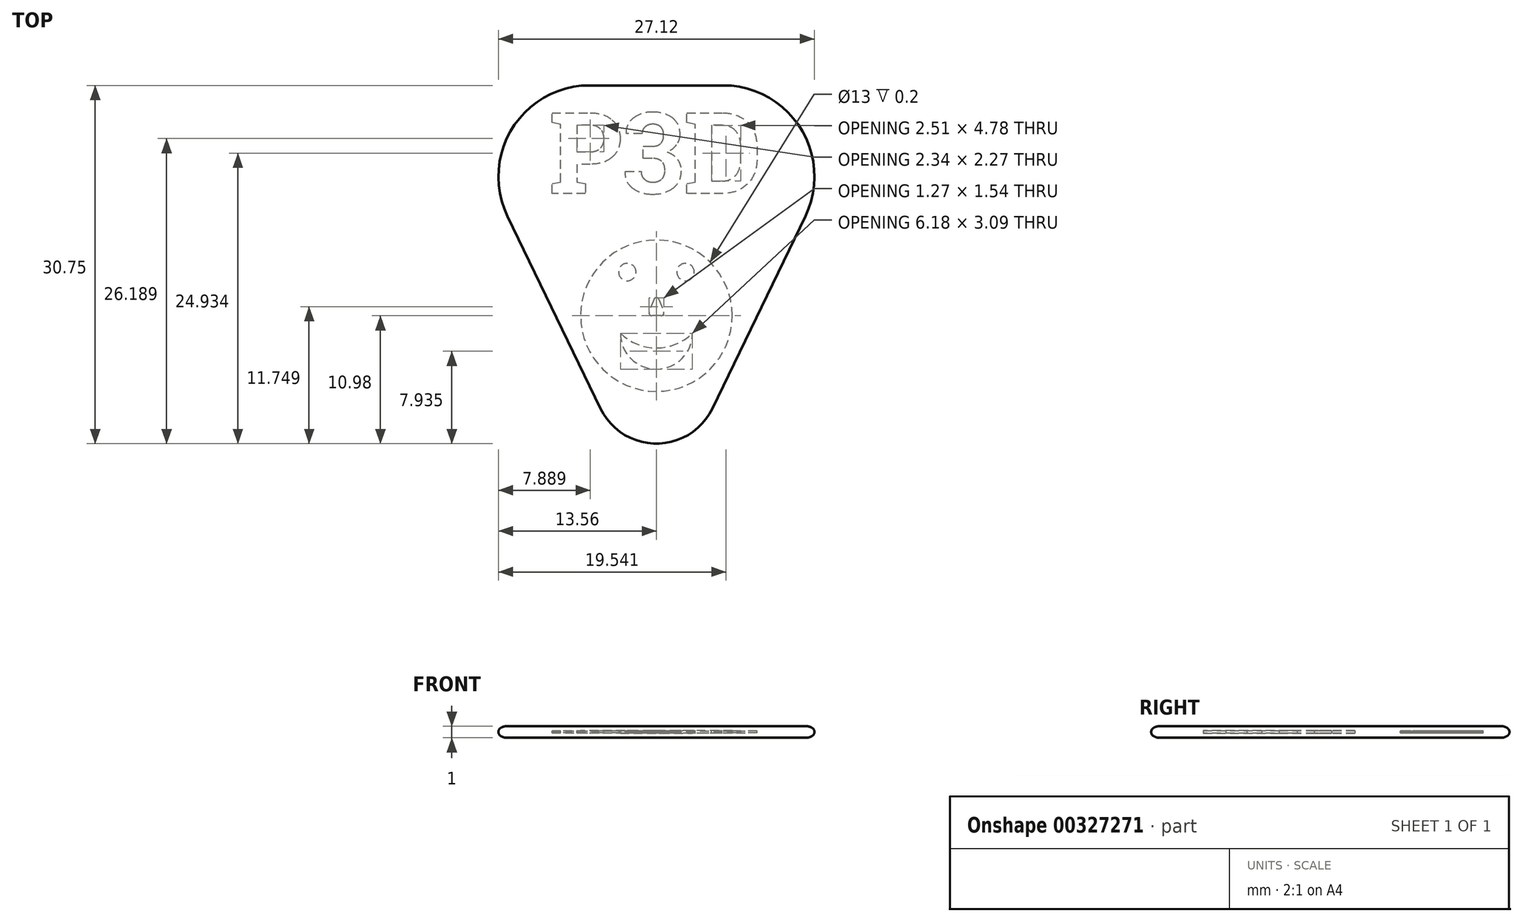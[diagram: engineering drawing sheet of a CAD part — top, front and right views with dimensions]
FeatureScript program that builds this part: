
annotation { "Feature Type Name" : "Feature", "Feature Type Description" : "" }
export const myFeature = defineFeature(function(context is Context, id is Id, definition is map)
    precondition{}
    {
        {
            var Q0;
            Q0=qCreatedBy(makeId("Top.planeOp"),FACE);
            var sketch = newSketch(context, id + "F0", { "sketchPlane" : qUnion([Q0])});
            skLineSegment(sketch, "E0", {"start": v(-5.74, 12.45) * mm, "end": v(5.74, 12.45) * mm});
            skLineSegment(sketch, "E1", {"start": v(12.95, 0.97) * mm, "end": v(4.95, -15.56) * mm});
            skLineSegment(sketch, "E2", {"start": v(-4.95, -15.56) * mm, "end": v(-12.95, 0.97) * mm});
            skPoint(sketch, "E3.visualSharp", {"position": v(-18.5, 12.45) * mm});
            skArc(sketch, "E3.filletArc", {"start": v(-5.74, 12.45) * mm, "mid": v(-12.52, 8.7) * mm, "end": v(-12.95, 0.97) * mm});
            skPoint(sketch, "E4.visualSharp", {"position": v(18.5, 12.45) * mm});
            skArc(sketch, "E4.filletArc", {"start": v(12.95, 0.97) * mm, "mid": v(12.52, 8.7) * mm, "end": v(5.74, 12.45) * mm});
            skPoint(sketch, "E5.visualSharp", {"position": v(0, -25.8) * mm});
            skArc(sketch, "E5.filletArc", {"start": v(-4.95, -15.56) * mm, "mid": v(0, -18.66) * mm, "end": v(4.95, -15.56) * mm});
            skSolve(sketch);
        }
        {
            var Q0;
            Q0=makeQuery(id+"F0.imprint","IMPRINT",FACE,{"disambiguationData":[TD([[makeQuery(id+"F0.imprint","IMPRINT",EDGE,{"derivedFrom":sQuery(id+"F0.wireOp",EDGE,"E0")}),-1.0]])]});
            extrude(context, id + "F1", {"entities" : qUnion([Q0]), "endBound" : BoundingType.SYMMETRIC, "depth" : 1 * mm, "offsetDistance" : 25 * mm});
        }
        {
            var Q0;
            Q0=makeQuery(id+"F1.opExtrude","CAP_EDGE",EDGE,{"disambiguationData":[OSD([sQuery(id+"F0.wireOp",EDGE,"E1")])],"isStart":false});
            var Q1;
            Q1=makeQuery(id+"F1.opExtrude","CAP_EDGE",EDGE,{"disambiguationData":[OSD([sQuery(id+"F0.wireOp",EDGE,"E1")])],"isStart":true});
            chamfer(context, id + "F2", {"entities" : qUnion([Q0, Q1]), "chamferType" : ChamferType.OFFSET_ANGLE, "width" : 0.5 * mm, "oppositeDirection" : false, "angle" : 45 * degree, "tangentPropagation" : true});
        }
        {
            var Q0;
            {var subQ0=sQuery(id+"F0.wireOp",EDGE,"E2");Q0=makeQuery(id+"F2.opChamfer","BLEND_EDGE",EDGE,{"blendedFrom":[makeQuery(id+"F1.opExtrude","CAP_EDGE",EDGE,{"disambiguationData":[OSD([subQ0])],"isStart":false}),makeQuery(id+"F1.opExtrude","CAP_FACE",FACE,{"disambiguationData":[OSD([sQuery(id+"F0.wireOp",EDGE,"E0"),sQuery(id+"F0.wireOp",EDGE,"E1"),subQ0,sQuery(id+"F0.wireOp",EDGE,"E3.filletArc"),sQuery(id+"F0.wireOp",EDGE,"E4.filletArc"),sQuery(id+"F0.wireOp",EDGE,"E5.filletArc")])],"isStart":false})],"blendedInto":[makeQuery(id+"F1.opExtrude","CAP_FACE",FACE,{"disambiguationData":[OSD([sQuery(id+"F0.wireOp",EDGE,"E0"),sQuery(id+"F0.wireOp",EDGE,"E1"),subQ0,sQuery(id+"F0.wireOp",EDGE,"E3.filletArc"),sQuery(id+"F0.wireOp",EDGE,"E4.filletArc"),sQuery(id+"F0.wireOp",EDGE,"E5.filletArc")])],"isStart":false})]});}
            var Q1;
            {var subQ0=sQuery(id+"F0.wireOp",EDGE,"E1");Q1=makeQuery(id+"F2.opChamfer","BLEND_EDGE",EDGE,{"blendedFrom":[makeQuery(id+"F1.opExtrude","CAP_EDGE",EDGE,{"disambiguationData":[OSD([subQ0])],"isStart":true}),makeQuery(id+"F1.opExtrude","CAP_FACE",FACE,{"disambiguationData":[OSD([sQuery(id+"F0.wireOp",EDGE,"E0"),subQ0,sQuery(id+"F0.wireOp",EDGE,"E2"),sQuery(id+"F0.wireOp",EDGE,"E3.filletArc"),sQuery(id+"F0.wireOp",EDGE,"E4.filletArc"),sQuery(id+"F0.wireOp",EDGE,"E5.filletArc")])],"isStart":true})],"blendedInto":[makeQuery(id+"F1.opExtrude","CAP_FACE",FACE,{"disambiguationData":[OSD([sQuery(id+"F0.wireOp",EDGE,"E0"),subQ0,sQuery(id+"F0.wireOp",EDGE,"E2"),sQuery(id+"F0.wireOp",EDGE,"E3.filletArc"),sQuery(id+"F0.wireOp",EDGE,"E4.filletArc"),sQuery(id+"F0.wireOp",EDGE,"E5.filletArc")])],"isStart":true})]});}
            fillet(context, id + "F3", {"entities" : qUnion([Q0, Q1]), "radius" : 1 * mm, "tangentPropagation" : true, "allowEdgeOverflow" : false});
        }
        {
            var Q0;
            Q0=qCreatedBy(makeId("Top.planeOp"),FACE);
            var sketch = newSketch(context, id + "F4", { "sketchPlane" : qUnion([Q0])});
            skText(sketch, "E6", { "text": "P3D", "fontName": "RobotoSlab-Bold.ttf"});
            const initialGuessF4  = {"E6": [-0.00923, 0.003, 1, 0, 0.007]};
            skSetInitialGuess(sketch, initialGuessF4);
            skSolve(sketch);
        }
        {
            var Q0;
            Q0=qSketchRegion(id+"F4",true);
            extrude(context, id + "F5", {"entities" : qUnion([Q0]), "operationType" : NewBodyOperationType.REMOVE, "endBound" : BoundingType.SYMMETRIC, "oppositeDirection" : true, "depth" : 0.18 * mm, "offsetDistance" : 25 * mm});
        }
        {
            var Q0;
            {var subQ0=sQuery(id+"F0.wireOp",EDGE,"E2");Q0=makeQuery(id+"F2.opChamfer","BLEND_EDGE",EDGE,{"blendedFrom":[makeQuery(id+"F1.opExtrude","CAP_EDGE",EDGE,{"disambiguationData":[OSD([subQ0])],"isStart":true}),makeQuery(id+"F1.opExtrude","CAP_EDGE",EDGE,{"disambiguationData":[OSD([subQ0])],"isStart":false})],"blendedInto":[]});}
            fillet(context, id + "F6", {"entities" : qUnion([Q0]), "radius" : 0.4 * mm, "tangentPropagation" : true, "allowEdgeOverflow" : false});
        }
        {
            var Q0;
            Q0=qCreatedBy(makeId("Top.planeOp"),FACE);
            var sketch = newSketch(context, id + "F7", { "sketchPlane" : qUnion([Q0])});
            skCircle(sketch, "E7", {"center": v(0, -7.5) * mm, "radius": 6.5 * mm});
            skCircle(sketch, "E8", {"center": v(-2.5, -3.75) * mm, "radius": 0.75 * mm});
            skCircle(sketch, "E9.MirrorC", {"center": v(2.5, -3.75) * mm, "radius": 0.75 * mm});
            skArc(sketch, "E10", {"start": v(-3.1, -9) * mm, "mid": v(0, -12.1) * mm, "end": v(3.1, -9) * mm});
            skLineSegment(sketch, "E11", {"start": v(-0.23, -6.12) * mm, "end": v(-0.62, -7.16) * mm});
            skLineSegment(sketch, "E12", {"start": v(-0.39, -7.5) * mm, "end": v(0, -7.5) * mm});
            skLineSegment(sketch, "E13.MirrorCS", {"start": v(0.23, -6.12) * mm, "end": v(0.62, -7.16) * mm});
            skLineSegment(sketch, "E14.MirrorCS", {"start": v(0.39, -7.5) * mm, "end": v(0, -7.5) * mm});
            skPoint(sketch, "E15.visualSharp", {"position": v(0, -5.5) * mm});
            skArc(sketch, "E15.filletArc", {"start": v(0.23, -6.12) * mm, "mid": v(0, -5.96) * mm, "end": v(-0.23, -6.12) * mm});
            skPoint(sketch, "E16.visualSharp", {"position": v(-0.75, -7.5) * mm});
            skArc(sketch, "E16.filletArc", {"start": v(-0.62, -7.16) * mm, "mid": v(-0.6, -7.4) * mm, "end": v(-0.39, -7.5) * mm});
            skPoint(sketch, "E17.visualSharp", {"position": v(0.75, -7.5) * mm});
            skArc(sketch, "E17.filletArc", {"start": v(0.39, -7.5) * mm, "mid": v(0.6, -7.4) * mm, "end": v(0.62, -7.16) * mm});
            skArc(sketch, "E18", {"start": v(-3.1, -9) * mm, "mid": v(0, -10.27) * mm, "end": v(3.1, -9) * mm});
            skSolve(sketch);
        }
        {
            var Q0;
            Q0=qSketchRegion(id+"F7",true);
            var Q1;
            Q1=makeQuery(id+"F7.imprint","IMPRINT",FACE,{"disambiguationData":[TD([[makeQuery(id+"F7.imprint","IMPRINT",EDGE,{"derivedFrom":sQuery(id+"F7.wireOp",EDGE,"939ed108-b3df-4f31-88ce-246f36476dcc.0")}),-1.0]])]});
            var Q2;
            Q2=makeQuery(id+"F7.imprint","IMPRINT",FACE,{"disambiguationData":[TD([[makeQuery(id+"F7.imprint","IMPRINT",EDGE,{"derivedFrom":sQuery(id+"F7.wireOp",EDGE,"7208b4ee-4551-4fd0-8a5f-77d057b4d0f6.0")}),-1.0]])]});
            extrude(context, id + "F8", {"entities" : qUnion([Q0, Q1, Q2]), "operationType" : NewBodyOperationType.REMOVE, "endBound" : BoundingType.SYMMETRIC, "depth" : 0.2 * mm, "offsetDistance" : 25 * mm});
        }
    });
